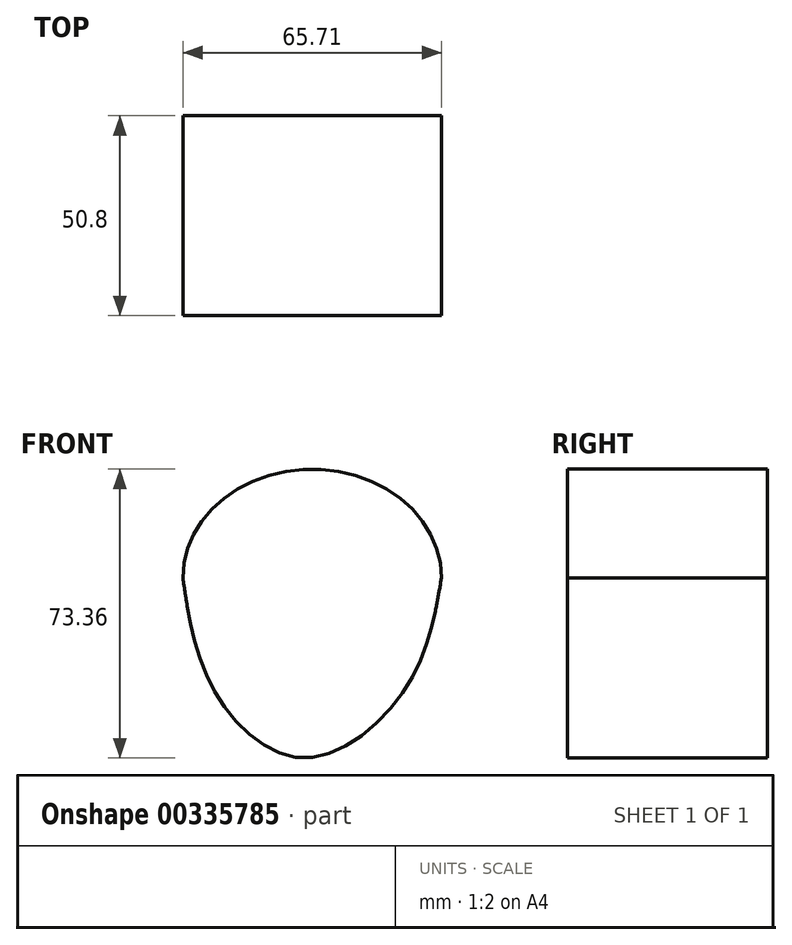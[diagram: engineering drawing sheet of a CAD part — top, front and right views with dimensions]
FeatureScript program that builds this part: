
annotation { "Feature Type Name" : "Feature", "Feature Type Description" : "" }
export const myFeature = defineFeature(function(context is Context, id is Id, definition is map)
    precondition{}
    {
        {
            var Q0;
            Q0=qCreatedBy(makeId("Front.planeOp"),FACE);
            var sketch = newSketch(context, id + "F0", { "sketchPlane" : qUnion([Q0])});
            skEllipse(sketch, "E0", {"center": v(-4.45, 38.44) * mm, "majorRadius": 32.85 * mm, "minorRadius": 27.61 * mm, "majorAxis": v(1, 0)});
            skPoint(sketch, "E1.3.internal.snap0", {"position": v(-4.45, 10.83) * mm});
            skFitSpline(sketch, "E1", {"points": [v(-37.3, 38.44) * mm, v(-28.96, 9.13) * mm, v(-6.21, -7.3) * mm, v(19.56, 10.83) * mm, v(28.4, 38.44) * mm], "startDerivative": vector(18.03, -119.95) * mm, "endDerivative": vector(19.5, 113.68) * mm});
            skSolve(sketch);
        }
        {
            var Q0;
            {var subQ0=sQuery(id+"F0.wireOp",EDGE,"E1");var subQ1=sQuery(id+"F0.wireOp",EDGE,"E0");var subQ2=makeQuery(id+"F0.imprint","INTERSECT",VERTEX,{"disambiguationData":[OD(0.0)],"derivedFrom":[subQ1,subQ0]});Q0=makeQuery(id+"F0.imprint","IMPRINT",FACE,{"disambiguationData":[TD([[makeQuery(id+"F0.imprint","IMPRINT",EDGE,{"disambiguationData":[TD([[subQ2,1.0]])],"derivedFrom":subQ1}),1.0]])]});}
            var Q1;
            {var subQ0=sQuery(id+"F0.wireOp",EDGE,"E1");var subQ1=sQuery(id+"F0.wireOp",EDGE,"E0");var subQ2=makeQuery(id+"F0.imprint","INTERSECT",VERTEX,{"disambiguationData":[OD(2.0)],"derivedFrom":[subQ1,subQ0]});Q1=makeQuery(id+"F0.imprint","IMPRINT",FACE,{"disambiguationData":[TD([[makeQuery(id+"F0.imprint","IMPRINT",EDGE,{"disambiguationData":[TD([[subQ2,-1.0]])],"derivedFrom":subQ1}),-1.0]])]});}
            extrude(context, id + "F1", {"entities" : qUnion([Q0, Q1]), "depth" : 50.8 * mm});
        }
    });
